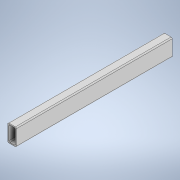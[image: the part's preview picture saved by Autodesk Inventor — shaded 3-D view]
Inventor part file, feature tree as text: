
AUTODESK INVENTOR PART (.ipt)
format: ipt  version: 2020 (Build 240168000, 168)  size: 120,320 bytes
history: native  units: in
note: dims shown in document units (in); Inventor stores cm internally (conversion verified against a paired STEP export)
features: extrude x1, sketch x1
ambient origin geometry x8: Origin, YZ Plane, XZ Plane, XY Plane, X Axis, Y Axis, Z Axis, Center Point
bodies: Solid1 (feature_tree)
feature tree (2):
  extrude  "Extrusion1"  Depth=1.0in
  sketch  "Sketch1"  dims[d0=2.0in d1=1.0in d2=0.125in d3=0.125in d4=0.125in d5=0.125in d6=0.125in d7=0.125in d8=0.125in d9=0.125in d10=0.125in d11=18.0in d12=0.0in]
